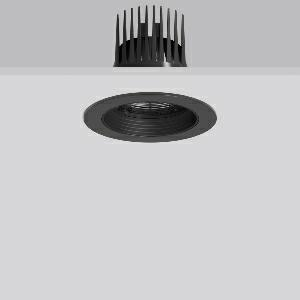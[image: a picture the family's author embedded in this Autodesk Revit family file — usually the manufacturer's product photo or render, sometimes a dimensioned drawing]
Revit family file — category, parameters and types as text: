
# Revit family: heledon_maxi_e_901762_003_2_76_3d74
name_source: partatom
category: Lighting Fixtures
units: mm (PartAtom-declared; Revit-internal decimal feet)

## family parameters
Cut with Voids When Loaded = No
Host = Face
Light Source = No
Part Type = Normal
Room Calculation Point = No
Round Connector Dimension = Use Diameter
Shared = No

## types (1)
- HELEDON maxi E (1 x LED Modul 927, 2650 lm, 2700)
    Apparent Load = 25 VA
    Approval mark = CE
    CIE Flux Codes = 96 100 100 100 100
    Color Rendering = 92
    Color Temperature = 2700
    Default Elevation = 1800 mm
    Description = Series: HELEDON maxi
Round recessed downlight. Housing: die-cast aluminium, powder-coated. Black plastic ring and recessed LED to prevent glare from the side. Optical assembly with lens made of plastic (polycarbonate) for the best homogeneous light distribution - can be changed without tools. Best colour rendering index Ra>90. Suitable for Recessed ceiling mounting. Installation without tools thanks to spring fastening system. Including separate LED converter with connecting cable 600 mm.High quality converter without flickering and stroboscopic effect. Through-wiring box (5 pole) available as accessory. The following accessories can be mounted without use of tools: interchangeable lenses, decorative glasses, honeycomb louvre, clear and frosted diffusers, white interchangeable plastic ring. 
Colour: deep black, matt (RAL 9005)
Diameter: 162 mm
Height: 3 mm
Cut-out diameter: 152 mm
Recess height: 200 mm
Luminaire: recess height: 135 mm
Lamp: LED
Socket: without socket
Colour temperature: 2700K
Colour rendering index (CRI): 92
System power: 25 W
Rated luminous flux: 2650 lm
Luminous efficiency: 106 lm/W
Control gear: Converter, dimmable, DALI
Protection class: II
Type of protection: IP 20
    Height = 0 mm  [stored 0 ft]
    Lamp = 1 x LED Modul 927
    Lamp Light Flux = 2650 lm
    Lamp count = 1
    Length = 162 mm
    Lifetime = 50000 h
    Luminous efficacy = 106 lm/W
    Manufacturer = RZB
    ModVariant = No
    Model = 901762.003.2.76
    Mounting Place = Ceiling
    Mounting Type = Recessed
    Number of Poles = 1
    OnlyDefault = Yes
    Power Factor = 1
    Product Name = HELEDON maxi E
    Product group = Recessed downlights
    ProductGroupID = 402
    Protection Class = Protection class II
    Protection Degree = IP 20
    RLX_Detail_Level = 1
    RLX_Emergency_Light_Flux = 0 lm
    RLX_Emergency_Type = 0
    RLX_Emergency_Type_DB = No
    RlxData = <blob elided: 121681 chars, md5=437058ef>
    Socket = socket
    Standby Power = 0 W
    System Light Flux = 2650 lm
    System Power = 25 W
    Type Comments = Product without accessories
    Type Image = 901663.003.jpg
    URL = http://relux.com
    VarID = ---
    Voltage = 230 V
    Voltage Range = 220-240 V
    Weight = 0.00 kg
    Width = 0 mm  [stored 0 ft]

note: [stored X ft] marks values corroborated as IEEE doubles in the binary element streams (Revit-internal decimal feet)

## geometry (parser evidence)
native form markers: Blend x4, Sweep x10
no freeform markers — native parametric forms only
